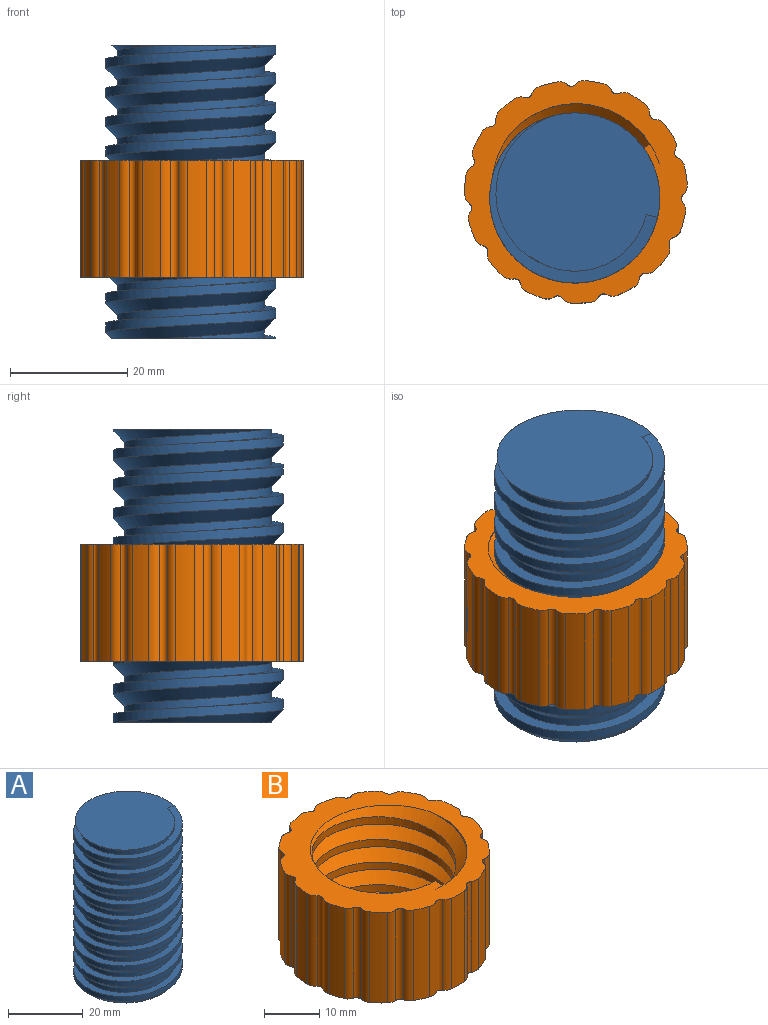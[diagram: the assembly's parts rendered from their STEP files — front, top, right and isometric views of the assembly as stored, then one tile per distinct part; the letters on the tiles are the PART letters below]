
ASSEMBLY  parts=2 mates=1
PART A: 6 faces, bbox 30.5x34.9x55.6 mm
  f0: cylinder r=12.5mm len=50mm, axis (0,0,-1), area 2018.4mm2, adj f1,f3,f4,f5
  f1: bspline ~53.99x28.97mm, area 2405.6mm2, adj f0,f2,f4,f5
  f2: bspline ~54.1x33.49mm, area 1461.7mm2, adj f1,f3,f4,f5
  f3: bspline ~50.83x33.49mm, area 1701.6mm2, adj f0,f2,f4,f5
  f4: plane 29.33x28.38mm, normal (0,0,-1), area 578.7mm2, adj f0,f1,f2,f3
  f5: plane 29.33x28.38mm, normal (0,0,1), area 578.7mm2, adj f0,f1,f2,f3
PART B: 66 faces, bbox 39.3x39.2x25.8 mm
  f0: cylinder r=2mm len=20mm, axis (0,0,1), area 36.2mm2, adj f2,f58,f60,f61
  f1: cylinder r=2mm len=20mm, axis (0,0,1), area 36.2mm2, adj f2,f59,f60,f61
  f2: cylinder r=1mm len=20mm, axis (0,0,-1), area 31.2mm2, adj f0,f1,f60,f61
  f3: cylinder r=2mm len=20mm, axis (0,0,1), area 36.2mm2, adj f5,f57,f60,f61
  f4: cylinder r=2mm len=20mm, axis (0,0,1), area 36.2mm2, adj f5,f58,f60,f61
  f5: cylinder r=1mm len=20mm, axis (0,0,-1), area 31.2mm2, adj f3,f4,f60,f61
  f6: cylinder r=2mm len=20mm, axis (0,0,1), area 36.2mm2, adj f8,f56,f60,f61
  f7: cylinder r=2mm len=20mm, axis (0,0,1), area 36.2mm2, adj f8,f57,f60,f61
  f8: cylinder r=1mm len=20mm, axis (0,0,-1), area 31.2mm2, adj f6,f7,f60,f61
  f9: cylinder r=2mm len=20mm, axis (0,0,1), area 36.2mm2, adj f11,f55,f60,f61
  f10: cylinder r=2mm len=20mm, axis (0,0,1), area 36.2mm2, adj f11,f56,f60,f61
  f11: cylinder r=1mm len=20mm, axis (0,0,-1), area 31.2mm2, adj f9,f10,f60,f61
  f12: cylinder r=2mm len=20mm, axis (0,0,1), area 36.2mm2, adj f14,f54,f60,f61
  f13: cylinder r=2mm len=20mm, axis (0,0,1), area 36.2mm2, adj f14,f55,f60,f61
  f14: cylinder r=1mm len=20mm, axis (0,0,-1), area 31.2mm2, adj f12,f13,f60,f61
  f15: cylinder r=2mm len=20mm, axis (0,0,1), area 36.2mm2, adj f17,f53,f60,f61
  f16: cylinder r=2mm len=20mm, axis (0,0,1), area 36.2mm2, adj f17,f54,f60,f61
  f17: cylinder r=1mm len=20mm, axis (0,0,-1), area 31.2mm2, adj f15,f16,f60,f61
  f18: cylinder r=2mm len=20mm, axis (0,0,1), area 36.2mm2, adj f20,f52,f60,f61
  f19: cylinder r=2mm len=20mm, axis (0,0,1), area 36.2mm2, adj f20,f53,f60,f61
  f20: cylinder r=1mm len=20mm, axis (0,0,-1), area 31.2mm2, adj f18,f19,f60,f61
  f21: cylinder r=2mm len=20mm, axis (0,0,1), area 36.2mm2, adj f23,f51,f60,f61
  f22: cylinder r=2mm len=20mm, axis (0,0,1), area 36.2mm2, adj f23,f52,f60,f61
  f23: cylinder r=1mm len=20mm, axis (0,0,-1), area 31.2mm2, adj f21,f22,f60,f61
  f24: cylinder r=2mm len=20mm, axis (0,0,1), area 36.2mm2, adj f26,f50,f60,f61
  f25: cylinder r=2mm len=20mm, axis (0,0,1), area 36.2mm2, adj f26,f51,f60,f61
  f26: cylinder r=1mm len=20mm, axis (0,0,-1), area 31.2mm2, adj f24,f25,f60,f61
  f27: cylinder r=2mm len=20mm, axis (0,0,1), area 36.2mm2, adj f29,f49,f60,f61
  f28: cylinder r=2mm len=20mm, axis (0,0,1), area 36.2mm2, adj f29,f50,f60,f61
  f29: cylinder r=1mm len=20mm, axis (0,0,-1), area 31.2mm2, adj f27,f28,f60,f61
  f30: cylinder r=2mm len=20mm, axis (0,0,1), area 36.2mm2, adj f32,f48,f60,f61
  f31: cylinder r=2mm len=20mm, axis (0,0,1), area 36.2mm2, adj f32,f49,f60,f61
  f32: cylinder r=1mm len=20mm, axis (0,0,-1), area 31.2mm2, adj f30,f31,f60,f61
  f33: cylinder r=2mm len=20mm, axis (0,0,1), area 36.2mm2, adj f35,f47,f60,f61
  f34: cylinder r=2mm len=20mm, axis (0,0,1), area 36.2mm2, adj f35,f48,f60,f61
  f35: cylinder r=1mm len=20mm, axis (0,0,-1), area 31.2mm2, adj f33,f34,f60,f61
  f36: cylinder r=2mm len=20mm, axis (0,0,1), area 36.2mm2, adj f38,f46,f60,f61
  f37: cylinder r=2mm len=20mm, axis (0,0,1), area 36.2mm2, adj f38,f47,f60,f61
  f38: cylinder r=1mm len=20mm, axis (0,0,-1), area 31.2mm2, adj f36,f37,f60,f61
  f39: cylinder r=2mm len=20mm, axis (0,0,1), area 36.2mm2, adj f41,f45,f60,f61
  f40: cylinder r=2mm len=20mm, axis (0,0,1), area 36.2mm2, adj f41,f46,f60,f61
  f41: cylinder r=1mm len=20mm, axis (0,0,-1), area 31.2mm2, adj f39,f40,f60,f61
  f42: cylinder r=2mm len=20mm, axis (0,0,1), area 36.2mm2, adj f44,f59,f60,f61
  f43: cylinder r=2mm len=20mm, axis (0,0,1), area 36.2mm2, adj f44,f45,f60,f61
  f44: cylinder r=1mm len=20mm, axis (0,0,-1), area 31.2mm2, adj f42,f43,f60,f61
  f45: cylinder r=19mm len=20mm, axis (0,0,-1), area 64.6mm2, adj f39,f43,f60,f61
  f46: cylinder r=19mm len=20mm, axis (0,0,-1), area 64.6mm2, adj f36,f40,f60,f61
  f47: cylinder r=19mm len=20mm, axis (0,0,-1), area 64.6mm2, adj f33,f37,f60,f61
  f48: cylinder r=19mm len=20mm, axis (0,0,-1), area 64.6mm2, adj f30,f34,f60,f61
  f49: cylinder r=19mm len=20mm, axis (0,0,-1), area 64.6mm2, adj f27,f31,f60,f61
  f50: cylinder r=19mm len=20mm, axis (0,0,-1), area 64.6mm2, adj f24,f28,f60,f61
  f51: cylinder r=19mm len=20mm, axis (0,0,-1), area 64.6mm2, adj f21,f25,f60,f61
  f52: cylinder r=19mm len=20mm, axis (0,0,-1), area 64.6mm2, adj f18,f22,f60,f61
  f53: cylinder r=19mm len=20mm, axis (0,0,-1), area 64.6mm2, adj f15,f19,f60,f61
  f54: cylinder r=19mm len=20mm, axis (0,0,-1), area 64.6mm2, adj f12,f16,f60,f61
  f55: cylinder r=19mm len=20mm, axis (0,0,-1), area 64.6mm2, adj f9,f13,f60,f61
  f56: cylinder r=19mm len=20mm, axis (0,0,-1), area 64.6mm2, adj f6,f10,f60,f61
  f57: cylinder r=19mm len=20mm, axis (0,0,-1), area 64.6mm2, adj f3,f7,f60,f61
  f58: cylinder r=19mm len=20mm, axis (0,0,-1), area 64.6mm2, adj f0,f4,f60,f61
  f59: cylinder r=19mm len=20mm, axis (0,0,-1), area 64.6mm2, adj f1,f42,f60,f61
  f60: plane 39.3x39.18mm, normal (0,0,-1), area 489.9mm2, adj f0,f1,f2,f3,f4,f5,f6,f7
  f61: plane 39.3x39.18mm, normal (0,0,1), area 489.9mm2, adj f0,f1,f2,f3,f4,f5,f6,f7
  f62: cylinder r=15mm len=30mm, axis (0,0,-1), area 499.1mm2, adj f60,f61,f63,f64
  f63: bspline ~34.64x30.1mm, area 705.4mm2, adj f60,f61,f62,f65
  f64: bspline ~34.64x30.12mm, area 997mm2, adj f60,f61,f62,f65
  f65: bspline ~30.02x26.1mm, area 524.2mm2, adj f60,f61,f63,f64
PLACE A t=(0,0,-50)mm fixed
PLACE B rot(axis=(0,0,1),122.5deg) t=(0.22,1.09,-15.27)mm
MATE cylindrical B.f45 <-> A.f5  axis (0,0,1) through (0.22,1.09,6.88)mm
